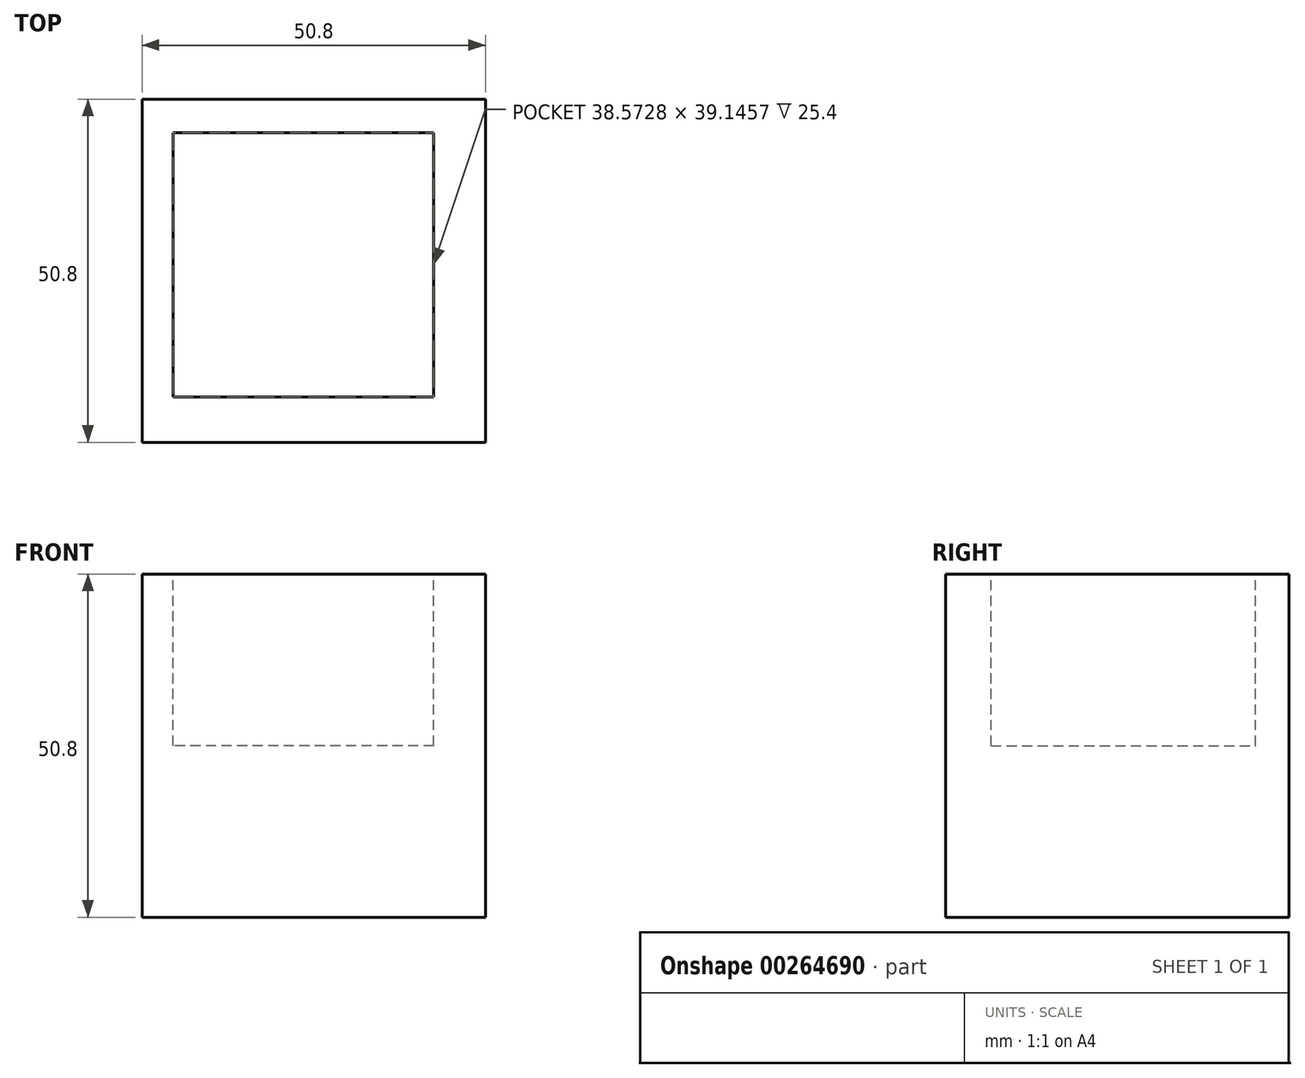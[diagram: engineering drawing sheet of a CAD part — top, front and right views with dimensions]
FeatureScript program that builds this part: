
annotation { "Feature Type Name" : "Feature", "Feature Type Description" : "" }
export const myFeature = defineFeature(function(context is Context, id is Id, definition is map)
    precondition{}
    {
        {
            var Q0;
            Q0=qCreatedBy(makeId("Front.planeOp"),FACE);
            var sketch = newSketch(context, id + "F0", { "sketchPlane" : qUnion([Q0])});
            skLineSegment(sketch, "E0.bottom", {"start": v(0, 0) * mm, "end": v(-50.8, 0) * mm});
            skLineSegment(sketch, "E0.top", {"start": v(0, 50.8) * mm, "end": v(-50.8, 50.8) * mm});
            skLineSegment(sketch, "E0.left", {"start": v(0, 0) * mm, "end": v(0, 50.8) * mm});
            skLineSegment(sketch, "E0.right", {"start": v(-50.8, 0) * mm, "end": v(-50.8, 50.8) * mm});
            skSolve(sketch);
        }
        {
            var Q0;
            Q0=makeQuery(id+"F0.imprint","IMPRINT",FACE,{"disambiguationData":[TD([[makeQuery(id+"F0.imprint","IMPRINT",EDGE,{"derivedFrom":sQuery(id+"F0.wireOp",EDGE,"E0.bottom")}),-1.0]])]});
            extrude(context, id + "F1", {"entities" : qUnion([Q0]), "depth" : 50.8 * mm});
        }
        {
            var Q0;
            Q0=makeQuery(id+"F1.opExtrude","SWEPT_FACE",FACE,{"disambiguationData":[OSD([sQuery(id+"F0.wireOp",EDGE,"E0.top")])]});
            var sketch = newSketch(context, id + "F2", { "sketchPlane" : qUnion([Q0])});
            skLineSegment(sketch, "E1.bottom", {"start": v(-7.64, -44.11) * mm, "end": v(-46.21, -44.11) * mm});
            skLineSegment(sketch, "E1.top", {"start": v(-7.64, -4.96) * mm, "end": v(-46.21, -4.96) * mm});
            skLineSegment(sketch, "E1.left", {"start": v(-7.64, -44.11) * mm, "end": v(-7.64, -4.96) * mm});
            skLineSegment(sketch, "E1.right", {"start": v(-46.21, -44.11) * mm, "end": v(-46.21, -4.96) * mm});
            skSolve(sketch);
        }
        {
            var Q0;
            Q0 = qSketchRegion(id + "F2", true);
            extrude(context, id + "F3", {"entities" : qUnion([Q0]), "operationType" : NewBodyOperationType.REMOVE, "oppositeDirection" : true, "depth" : 25.4 * mm});
        }
    });
